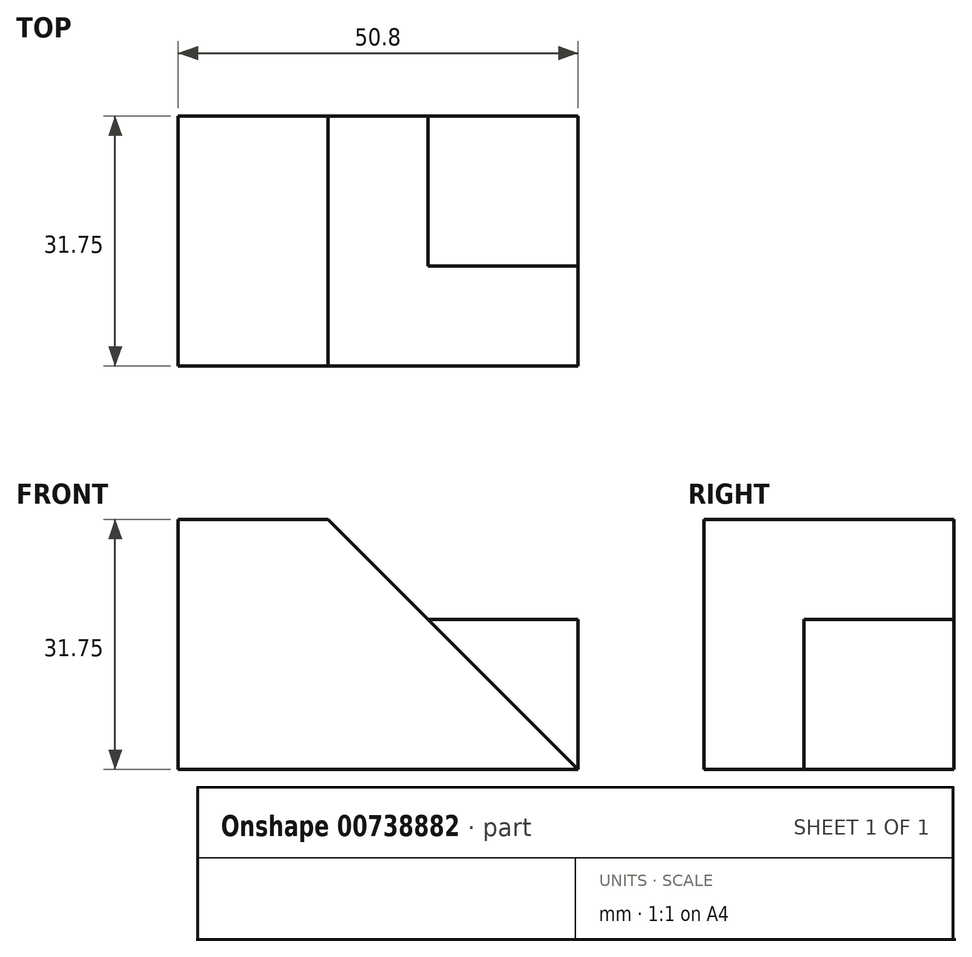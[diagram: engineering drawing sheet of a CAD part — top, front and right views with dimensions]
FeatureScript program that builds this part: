
annotation { "Feature Type Name" : "Feature", "Feature Type Description" : "" }
export const myFeature = defineFeature(function(context is Context, id is Id, definition is map)
    precondition{}
    {
        {
            var Q0;
            Q0=qCreatedBy(makeId("Front.planeOp"),FACE);
            var sketch = newSketch(context, id + "F0", { "sketchPlane" : qUnion([Q0])});
            skLineSegment(sketch, "E0", {"start": v(0, 0) * mm, "end": v(50.8, 0) * mm});
            skLineSegment(sketch, "E1", {"start": v(50.8, 0) * mm, "end": v(50.8, 31.75) * mm});
            skLineSegment(sketch, "E2", {"start": v(50.8, 31.75) * mm, "end": v(0, 31.75) * mm});
            skLineSegment(sketch, "E3", {"start": v(0, 31.75) * mm, "end": v(0, 0) * mm});
            skSolve(sketch);
        }
        {
            var Q0;
            Q0 = qSketchRegion(id + "F0", true);
            extrude(context, id + "F1", {"entities" : qUnion([Q0]), "depth" : 31.75 * mm, "offsetDistance" : 25.4 * mm});
        }
        {
            var Q0;
            Q0=makeQuery(id+"F1.opExtrude","CAP_FACE",FACE,{"disambiguationData":[OSD([sQuery(id+"F0.wireOp",EDGE,"E0"),sQuery(id+"F0.wireOp",EDGE,"E1"),sQuery(id+"F0.wireOp",EDGE,"E2"),sQuery(id+"F0.wireOp",EDGE,"E3")])],"isStart":false});
            var sketch = newSketch(context, id + "F2", { "sketchPlane" : qUnion([Q0])});
            skLineSegment(sketch, "E4", {"start": v(19.05, 31.75) * mm, "end": v(50.8, 0) * mm});
            skSolve(sketch);
        }
        {
            var Q0;
            Q0 = qSketchRegion(id + "F2", true);
            var Q1;
            {var subQ0=sQuery(id+"F2.wireOp",EDGE,"E4");Q1=makeQuery(id+"F2.imprint","IMPRINT",FACE,{"disambiguationData":[TD([[makeQuery(id+"F2.imprint","IMPRINT",EDGE,{"derivedFrom":subQ0}),1.0]])]});}
            extrude(context, id + "F3", {"entities" : qUnion([Q0, Q1]), "operationType" : NewBodyOperationType.REMOVE, "oppositeDirection" : true, "depth" : 12.7 * mm, "offsetDistance" : 25.4 * mm});
        }
        {
            var Q0;
            Q0=makeQuery(id+"F3.boolean.opBoolean","COPY",FACE,{"derivedFrom":makeQuery(id+"F3.opExtrude","CAP_FACE",FACE,{"disambiguationData":[OSD([sQuery(id+"F0.wireOp",EDGE,"E1"),sQuery(id+"F0.wireOp",EDGE,"E2"),sQuery(id+"F2.wireOp",EDGE,"E4")])],"isStart":false})});
            var sketch = newSketch(context, id + "F4", { "sketchPlane" : qUnion([Q0])});
            skLineSegment(sketch, "E5", {"start": v(31.75, 19.05) * mm, "end": v(50.8, 19.05) * mm});
            skSolve(sketch);
        }
        {
            var Q0;
            Q0 = qSketchRegion(id + "F4", true);
            var Q1;
            {var subQ0=sQuery(id+"F4.wireOp",EDGE,"E5");Q1=makeQuery(id+"F4.imprint","IMPRINT",FACE,{"disambiguationData":[TD([[makeQuery(id+"F4.imprint","IMPRINT",EDGE,{"derivedFrom":subQ0}),1.0]])]});}
            extrude(context, id + "F5", {"entities" : qUnion([Q0, Q1]), "operationType" : NewBodyOperationType.REMOVE, "oppositeDirection" : true, "depth" : 25.4 * mm, "offsetDistance" : 25.4 * mm});
        }
    });
